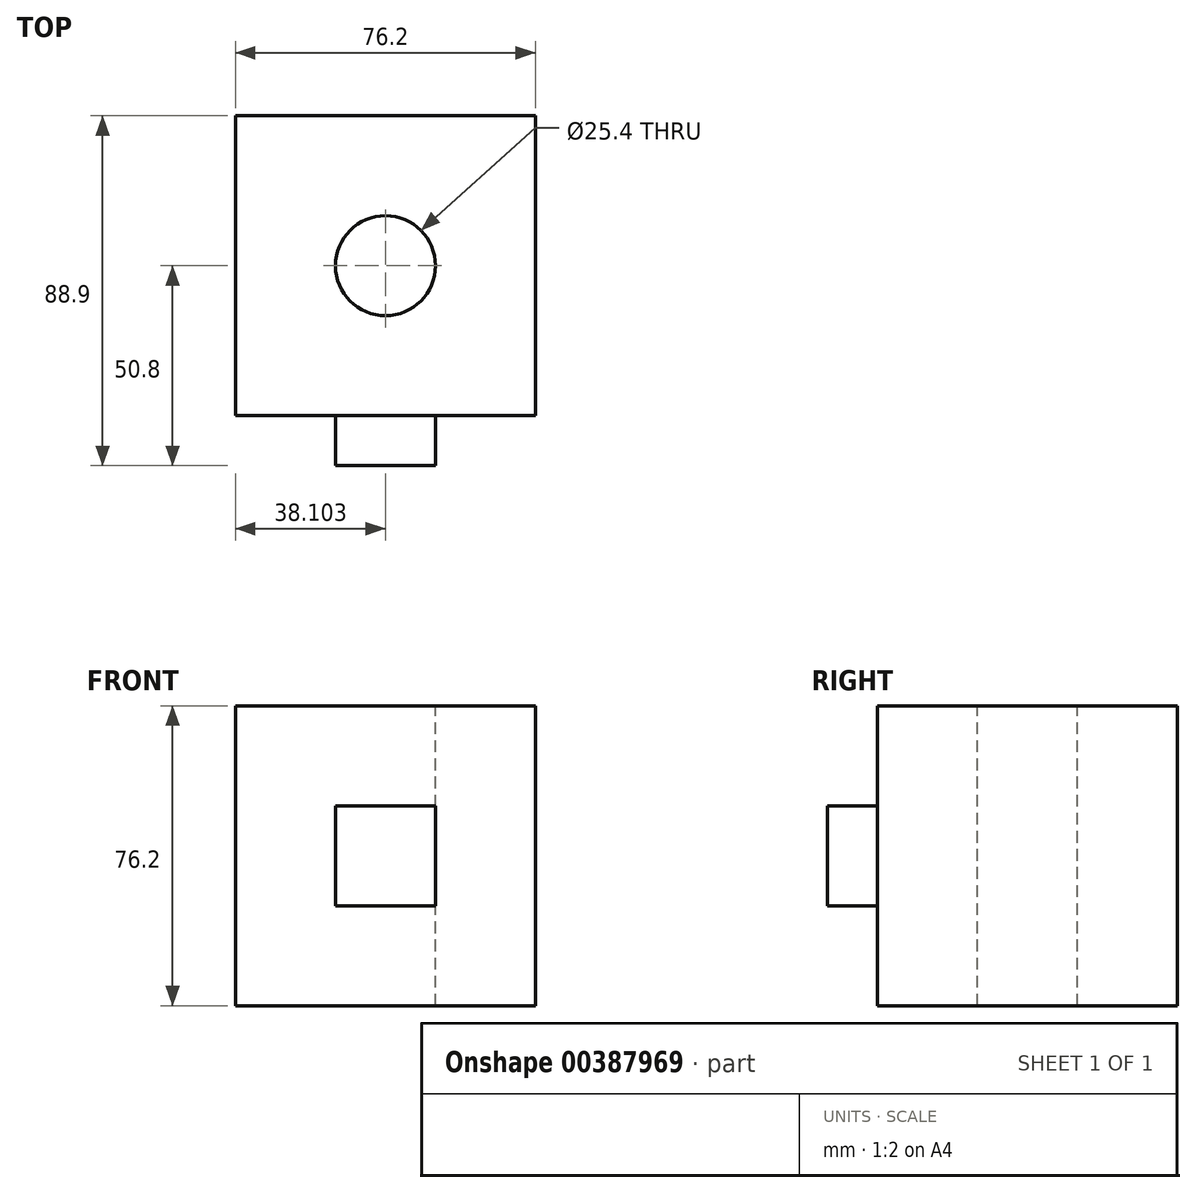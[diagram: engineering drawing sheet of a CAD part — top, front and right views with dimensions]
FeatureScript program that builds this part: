
annotation { "Feature Type Name" : "Feature", "Feature Type Description" : "" }
export const myFeature = defineFeature(function(context is Context, id is Id, definition is map)
    precondition{}
    {
        {
            var Q0;
            Q0=qCreatedBy(makeId("Front.planeOp"),FACE);
            var sketch = newSketch(context, id + "F0", { "sketchPlane" : qUnion([Q0])});
            skLineSegment(sketch, "E0.bottom", {"start": v(-40.3, 30.45) * mm, "end": v(35.9, 30.45) * mm});
            skLineSegment(sketch, "E0.top", {"start": v(-40.3, -45.75) * mm, "end": v(35.9, -45.75) * mm});
            skLineSegment(sketch, "E0.left", {"start": v(-40.3, 30.45) * mm, "end": v(-40.3, -45.75) * mm});
            skLineSegment(sketch, "E0.right", {"start": v(35.9, 30.45) * mm, "end": v(35.9, -45.75) * mm});
            skSolve(sketch);
        }
        {
            var Q0;
            Q0 = qSketchRegion(id + "F0", true);
            extrude(context, id + "F1", {"entities" : qUnion([Q0]), "depth" : 76.2 * mm});
        }
        {
            var Q0;
            Q0=makeQuery(id+"F1.opExtrude","SWEPT_FACE",FACE,{"disambiguationData":[OSD([sQuery(id+"F0.wireOp",EDGE,"E0.bottom")])]});
            var sketch = newSketch(context, id + "F2", { "sketchPlane" : qUnion([Q0])});
            skPoint(sketch, "E1", {"position": v(-2.2, -38.1) * mm});
            skPoint(sketch, "E2", {"position": v(-2.2, 0) * mm});
            skSolve(sketch);
        }
        {
            var Q0;
            Q0=sQuery(id+"F2.wireOp",VERTEX,"E1");
            var Q1;
            Q1=makeQuery(id+"F1.opExtrude","SWEPT_BODY",BODY,{"disambiguationData":[OSD([sQuery(id+"F0.wireOp",EDGE,"E0.bottom"),sQuery(id+"F0.wireOp",EDGE,"E0.top"),sQuery(id+"F0.wireOp",EDGE,"E0.left"),sQuery(id+"F0.wireOp",EDGE,"E0.right")])]});
            hole(context, id + "F3", {"style" : HoleStyle.SIMPLE, "endStyle" : HoleEndStyle.THROUGH, "holeDiameter" : 25.4 * mm, "isTappedThrough" : true, "tappedDepth" : 12.7 * mm, "tapClearance" : 3, "locations" : qUnion([Q0]), "scope" : qUnion([Q1])});
        }
        {
            var Q0;
            Q0=makeQuery(id+"F1.opExtrude","CAP_FACE",FACE,{"disambiguationData":[OSD([sQuery(id+"F0.wireOp",EDGE,"E0.bottom"),sQuery(id+"F0.wireOp",EDGE,"E0.top"),sQuery(id+"F0.wireOp",EDGE,"E0.left"),sQuery(id+"F0.wireOp",EDGE,"E0.right")])],"isStart":false});
            var sketch = newSketch(context, id + "F4", { "sketchPlane" : qUnion([Q0])});
            skLineSegment(sketch, "E3.bottom", {"start": v(-19.12, -4.48) * mm, "end": v(-19.12, -4.48) * mm});
            skLineSegment(sketch, "E4.bottom", {"start": v(-14.9, 5.05) * mm, "end": v(10.5, 5.05) * mm});
            skLineSegment(sketch, "E4.top", {"start": v(-14.9, -20.35) * mm, "end": v(10.5, -20.35) * mm});
            skLineSegment(sketch, "E4.left", {"start": v(-14.9, 5.05) * mm, "end": v(-14.9, -20.35) * mm});
            skLineSegment(sketch, "E4.right", {"start": v(10.5, 5.05) * mm, "end": v(10.5, -20.35) * mm});
            skSolve(sketch);
        }
        {
            var Q0;
            Q0=makeQuery(id+"F4.imprint","IMPRINT",FACE,{"disambiguationData":[TD([[makeQuery(id+"F4.imprint","IMPRINT",EDGE,{"derivedFrom":sQuery(id+"F4.wireOp",EDGE,"E4.bottom")}),-1.0]])]});
            extrude(context, id + "F5", {"entities" : qUnion([Q0]), "operationType" : NewBodyOperationType.ADD, "depth" : 12.7 * mm});
        }
    });
